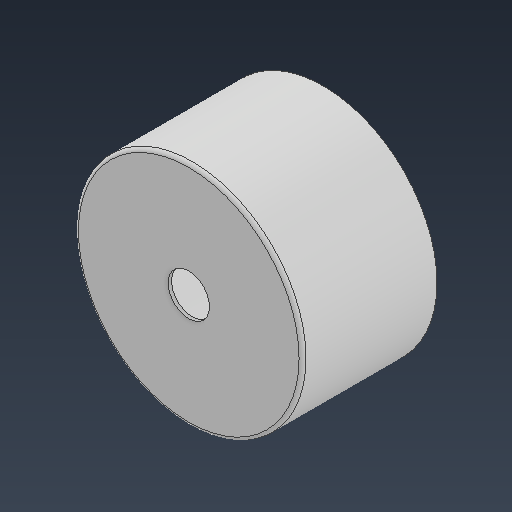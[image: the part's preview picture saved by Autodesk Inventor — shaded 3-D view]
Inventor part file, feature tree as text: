
AUTODESK INVENTOR PART (.ipt)
format: ipt  version: 2021 (Build 250183000, 183)  size: 102,912 bytes
history: native  units: in
note: dims shown in document units (in); Inventor stores cm internally (conversion verified against a paired STEP export)
features: fillet x1
ambient origin geometry x8: Origin, YZ Plane, XZ Plane, XY Plane, X Axis, Y Axis, Z Axis, Center Point
bodies: Solid1 (feature_tree)
feature tree (1):
  fillet  "Fillet1"  [1 undecoded]
note: 1 required parameter value undecoded (feature->parameter linkage not recoverable at this tier; creation-order binding heuristic only, values carry confidence <= 0.55)
